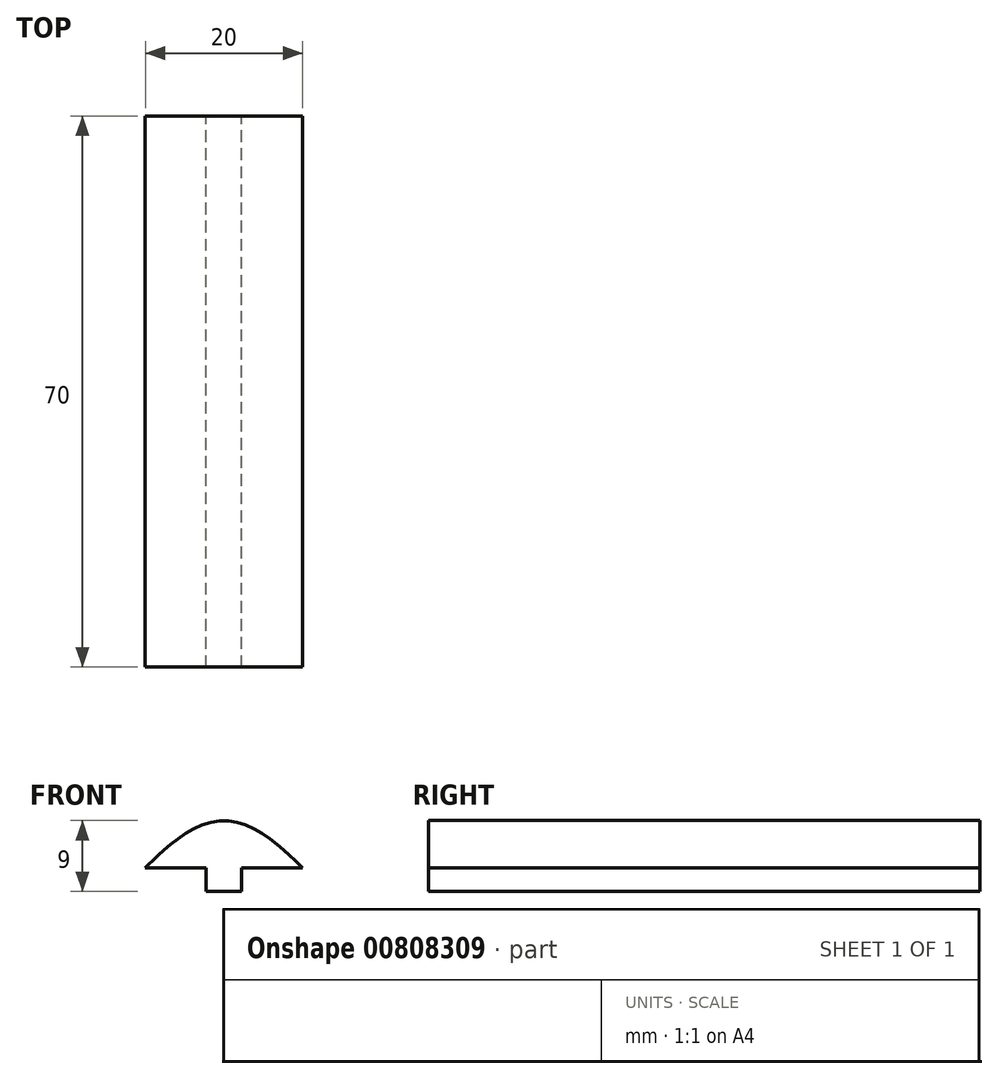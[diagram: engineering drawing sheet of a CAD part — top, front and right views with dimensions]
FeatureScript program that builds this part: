
annotation { "Feature Type Name" : "Feature", "Feature Type Description" : "" }
export const myFeature = defineFeature(function(context is Context, id is Id, definition is map)
    precondition{}
    {
        {
            var Q0;
            Q0=qCreatedBy(makeId("Front.planeOp"),FACE);
            var sketch = newSketch(context, id + "F0", { "sketchPlane" : qUnion([Q0])});
            skLineSegment(sketch, "E0", {"start": v(5.98, 0) * mm, "end": v(1.48, 0) * mm});
            skLineSegment(sketch, "E1", {"start": v(1.48, 0) * mm, "end": v(1.48, 3) * mm});
            skLineSegment(sketch, "E2", {"start": v(1.48, 3) * mm, "end": v(-6.27, 3) * mm});
            skLineSegment(sketch, "E3", {"start": v(5.98, 0) * mm, "end": v(5.98, 3) * mm});
            skLineSegment(sketch, "E4", {"start": v(5.98, 3) * mm, "end": v(13.73, 3) * mm});
            skFitSpline(sketch, "E5", {"points": [v(13.73, 3) * mm, v(3.73, 9) * mm, v(-6.27, 3) * mm], "startDerivative": vector(-8.95, 8.23) * mm, "endDerivative": vector(-8.06, -8.33) * mm});
            skPoint(sketch, "E6", {"position": v(3.73, 0) * mm});
            skSolve(sketch);
        }
        {
            var Q0;
            Q0=makeQuery(id+"F0.imprint","IMPRINT",FACE,{"disambiguationData":[TD([[makeQuery(id+"F0.imprint","IMPRINT",EDGE,{"derivedFrom":sQuery(id+"F0.wireOp",EDGE,"E0")}),-1.0]])]});
            extrude(context, id + "F1", {"entities" : qUnion([Q0]), "depth" : 70 * mm, "offsetDistance" : 25 * mm});
        }
    });
